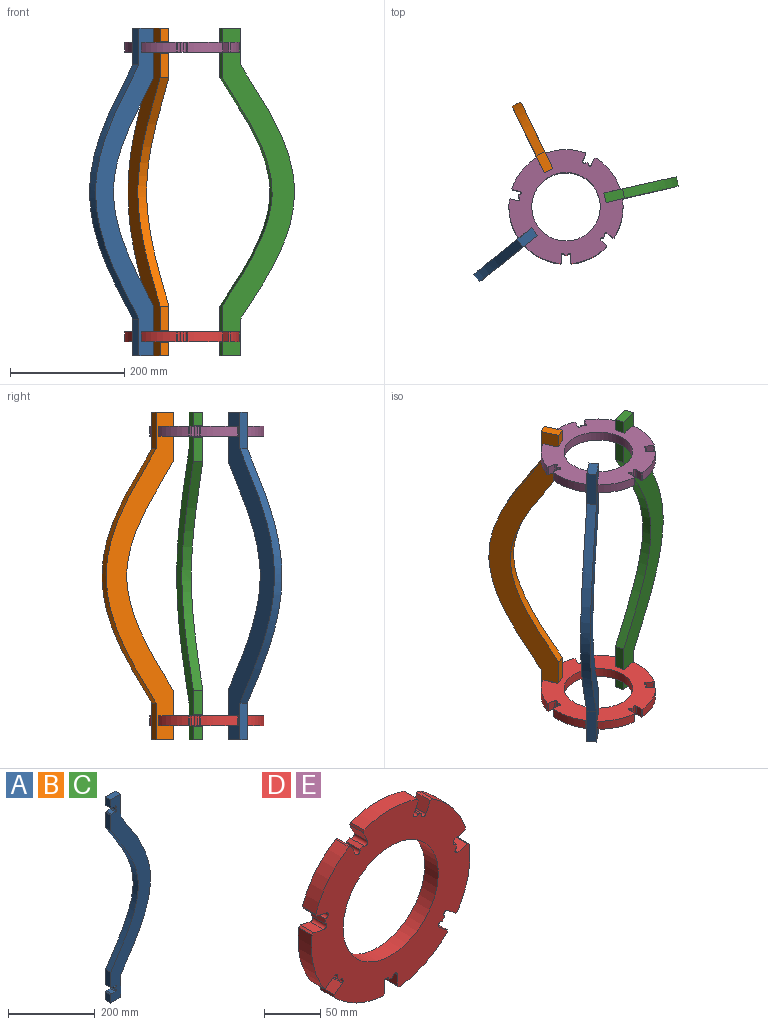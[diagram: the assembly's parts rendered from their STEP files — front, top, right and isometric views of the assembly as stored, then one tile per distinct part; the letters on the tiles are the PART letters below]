
ASSEMBLY  parts=5 mates=12
PART A: 26 faces, bbox 130x17x573.6 mm
  f0: plane 17x4.8mm, normal (-1,0,0), area 81.6mm2, adj f2,f3,f18,f19
  f1: plane 17x4.8mm, normal (-1,0,0), area 81.6mm2, adj f2,f3,f20,f21
  f2: plane 573.6x130.01mm, normal (0,-1,0), area 23198mm2, adj f0,f1,f4,f5,f6,f7,f8,f9
  f3: plane 573.6x130.01mm, normal (0,1,0), area 23198mm2, adj f0,f1,f4,f5,f6,f7,f8,f9
  f4: plane 33.15x17mm, normal (0,0,1), area 563.6mm2, adj f2,f3,f5,f17
  f5: plane 23x17mm, normal (-1,0,0), area 391mm2, adj f2,f3,f4,f25
  f6: plane 17x13mm, normal (0,0,-1), area 221mm2, adj f2,f3,f19,f25
  f7: plane 17x13mm, normal (0,0,1), area 221mm2, adj f2,f3,f18,f24
  f8: plane 43x17mm, normal (-1,0,0), area 731mm2, adj f2,f3,f9,f24
  f9: extruded ~400x90mm, area 7565.6mm2, adj f2,f3,f8,f10
  f10: plane 43x17mm, normal (-1,0,0), area 731mm2, adj f2,f3,f9,f23
  f11: plane 17x13mm, normal (0,0,-1), area 221mm2, adj f2,f3,f20,f23
  f12: plane 17x13mm, normal (0,0,1), area 221mm2, adj f2,f3,f21,f22
  f13: plane 23x17mm, normal (-1,0,0), area 391mm2, adj f2,f3,f14,f22
  f14: plane 33.15x17mm, normal (0,0,-1), area 563.6mm2, adj f2,f3,f13,f15
  f15: plane 64.42x17mm, normal (1,0,0), area 1095.2mm2, adj f2,f3,f14,f16
  f16: extruded ~444.76x96.85mm, area 8370.8mm2, adj f2,f3,f15,f17
  f17: plane 64.42x17mm, normal (1,0,0), area 1095.2mm2, adj f2,f3,f4,f16
  f18: cylinder r=3mm len=17mm, axis (0,-1,0), area 160.2mm2, adj f0,f2,f3,f7
  f19: cylinder r=3mm len=17mm, axis (0,-1,0), area 160.2mm2, adj f0,f2,f3,f6
  f20: cylinder r=3mm len=17mm, axis (0,-1,0), area 160.2mm2, adj f1,f2,f3,f11
  f21: cylinder r=3mm len=17mm, axis (0,-1,0), area 160.2mm2, adj f1,f2,f3,f12
  f22: plane 17x2mm, normal (-0.71,0,0.71), area 48.1mm2, adj f2,f3,f12,f13
  f23: plane 17x2mm, normal (-0.71,0,-0.71), area 48.1mm2, adj f2,f3,f10,f11
  f24: plane 17x2mm, normal (-0.71,0,0.71), area 48.1mm2, adj f2,f3,f7,f8
  f25: plane 17x2mm, normal (-0.71,0,-0.71), area 48.1mm2, adj f2,f3,f5,f6
PART B: same geometry as A
PART C: same geometry as A
PART D: 59 faces, bbox 200x17x199.5 mm
  f0: plane 17x3.75mm, normal (-0.78,0,-0.62), area 81.6mm2, adj f7,f8,f51,f58
  f1: plane 17x4.8mm, normal (0,0,-1), area 81.6mm2, adj f7,f8,f56,f57
  f2: plane 17x3.75mm, normal (0.78,0,-0.62), area 81.6mm2, adj f7,f8,f49,f55
  f3: plane 17x4.68mm, normal (0.97,0,0.22), area 81.6mm2, adj f7,f8,f47,f48
  f4: plane 17x4.32mm, normal (0.43,0,0.9), area 81.6mm2, adj f7,f8,f46,f50
  f5: plane 17x4.32mm, normal (-0.43,0,0.9), area 81.6mm2, adj f7,f8,f45,f54
  f6: plane 17x4.68mm, normal (-0.97,0,0.22), area 81.6mm2, adj f7,f8,f52,f53
  f7: plane 200x199.45mm, normal (0,-1,0), area 18129.3mm2, adj f0,f1,f2,f3,f4,f5,f6,f9
  f8: plane 200x199.45mm, normal (0,1,0), area 18129.3mm2, adj f0,f1,f2,f3,f4,f5,f6,f9
  f9: plane 17x12.31mm, normal (0.22,0,0.97), area 214.6mm2, adj f7,f8,f31,f53
  f10: cylinder r=100mm len=65.82mm, axis (0,1,0), area 1170.6mm2, adj f7,f8,f31,f33
  f11: plane 17x9.87mm, normal (0.62,0,-0.78), area 214.6mm2, adj f7,f8,f33,f58
  f12: plane 17x9.87mm, normal (-0.62,0,0.78), area 214.6mm2, adj f7,f8,f34,f51
  f13: cylinder r=100mm len=60.82mm, axis (0,1,0), area 1170.6mm2, adj f7,f8,f34,f35
  f14: plane 17x12.63mm, normal (1,0,0), area 214.6mm2, adj f7,f8,f35,f56
  f15: plane 17x12.63mm, normal (-1,0,0), area 214.6mm2, adj f7,f8,f36,f57
  f16: cylinder r=100mm len=60.82mm, axis (0,1,0), area 1170.6mm2, adj f7,f8,f36,f37
  f17: plane 17x9.87mm, normal (0.62,0,0.78), area 214.6mm2, adj f7,f8,f37,f49
  f18: plane 17x9.87mm, normal (-0.62,0,-0.78), area 214.6mm2, adj f7,f8,f38,f55
  f19: cylinder r=100mm len=65.82mm, axis (0,1,0), area 1170.6mm2, adj f7,f8,f38,f39
  f20: plane 17x12.31mm, normal (-0.22,0,0.97), area 214.6mm2, adj f7,f8,f39,f47
  f21: plane 17x12.31mm, normal (0.22,0,-0.97), area 214.6mm2, adj f7,f8,f40,f48
  f22: cylinder r=100mm len=52.78mm, axis (0,1,0), area 1170.6mm2, adj f7,f8,f40,f41
  f23: plane 17x11.38mm, normal (-0.9,0,0.43), area 214.6mm2, adj f7,f8,f41,f50
  f24: plane 17x11.38mm, normal (0.9,0,-0.43), area 214.6mm2, adj f7,f8,f42,f46
  f25: cylinder r=100mm len=67.51mm, axis (0,1,0), area 1170.6mm2, adj f7,f8,f42,f43
  f26: plane 17x11.38mm, normal (-0.9,0,-0.43), area 214.6mm2, adj f7,f8,f43,f54
  f27: plane 17x11.38mm, normal (0.9,0,0.43), area 214.6mm2, adj f7,f8,f44,f45
  f28: cylinder r=100mm len=52.78mm, axis (0,1,0), area 1170.6mm2, adj f7,f8,f32,f44
  f29: plane 17x12.31mm, normal (-0.22,0,-0.97), area 214.6mm2, adj f7,f8,f32,f52
  f30: cylinder r=60mm len=120mm, axis (0,1,0), area 6408.8mm2, adj f7,f8
  f31: plane 17x2.23mm, normal (-0.58,0,0.82), area 46.4mm2, adj f7,f8,f9,f10
  f32: plane 17x2.39mm, normal (-0.87,0,-0.49), area 46.4mm2, adj f7,f8,f28,f29
  f33: plane 17x2.7mm, normal (-0.16,0,-0.99), area 46.4mm2, adj f7,f8,f10,f11
  f34: plane 17x2.73mm, normal (-1,0,0.06), area 46.4mm2, adj f7,f8,f12,f13
  f35: plane 17x2.03mm, normal (0.67,0,-0.74), area 46.4mm2, adj f7,f8,f13,f14
  f36: plane 17x2.03mm, normal (-0.67,0,-0.74), area 46.4mm2, adj f7,f8,f15,f16
  f37: plane 17x2.73mm, normal (1,0,0.06), area 46.4mm2, adj f7,f8,f16,f17
  f38: plane 17x2.7mm, normal (0.16,0,-0.99), area 46.4mm2, adj f7,f8,f18,f19
  f39: plane 17x2.23mm, normal (0.58,0,0.82), area 46.4mm2, adj f7,f8,f19,f20
  f40: plane 17x2.39mm, normal (0.87,0,-0.49), area 46.4mm2, adj f7,f8,f21,f22
  f41: plane 17x2.62mm, normal (-0.28,0,0.96), area 46.4mm2, adj f7,f8,f22,f23
  f42: plane 17x2.53mm, normal (0.93,0,0.38), area 46.4mm2, adj f7,f8,f24,f25
  f43: plane 17x2.53mm, normal (-0.93,0,0.38), area 46.4mm2, adj f7,f8,f25,f26
  f44: plane 17x2.62mm, normal (0.28,0,0.96), area 46.4mm2, adj f7,f8,f27,f28
  f45: cylinder r=3mm len=17mm, axis (0,-1,0), area 160.2mm2, adj f5,f7,f8,f27
  f46: cylinder r=3mm len=17mm, axis (0,-1,0), area 160.2mm2, adj f4,f7,f8,f24
  f47: cylinder r=3mm len=17mm, axis (0,-1,0), area 160.2mm2, adj f3,f7,f8,f20
  f48: cylinder r=3mm len=17mm, axis (0,-1,0), area 160.2mm2, adj f3,f7,f8,f21
  f49: cylinder r=3mm len=17mm, axis (0,-1,0), area 160.2mm2, adj f2,f7,f8,f17
  f50: cylinder r=3mm len=17mm, axis (0,-1,0), area 160.2mm2, adj f4,f7,f8,f23
  f51: cylinder r=3mm len=17mm, axis (0,-1,0), area 160.2mm2, adj f0,f7,f8,f12
  f52: cylinder r=3mm len=17mm, axis (0,-1,0), area 160.2mm2, adj f6,f7,f8,f29
  f53: cylinder r=3mm len=17mm, axis (0,-1,0), area 160.2mm2, adj f6,f7,f8,f9
  f54: cylinder r=3mm len=17mm, axis (0,-1,0), area 160.2mm2, adj f5,f7,f8,f26
  f55: cylinder r=3mm len=17mm, axis (0,-1,0), area 160.2mm2, adj f2,f7,f8,f18
  f56: cylinder r=3mm len=17mm, axis (0,-1,0), area 160.2mm2, adj f1,f7,f8,f14
  f57: cylinder r=3mm len=17mm, axis (0,-1,0), area 160.2mm2, adj f1,f7,f8,f15
  f58: cylinder r=3mm len=17mm, axis (0,-1,0), area 160.2mm2, adj f0,f7,f8,f11
PART E: same geometry as D
PLACE A rot(axis=(0,0,-1),141.4deg) t=(-365.21,-119.31,119.36)mm
PLACE B rot(axis=(0,0,1),115.7deg) t=(-353.84,-9.76,119.36)mm
PLACE C rot(axis=(0,0,1),12.9deg) t=(-249.39,-45.14,119.36)mm
PLACE D rot(axis=(-0.83,-0.4,0.4),100.9deg) t=(-315.72,-69.1,-142.44)mm
PLACE E rot(axis=(-1,0,0),90deg) t=(-315.72,-69.1,364.16)mm
MATE planar B.f2 <-> E.f26  axis (0.9,0.43,0) through (-352.91,27.49,341.74)mm
MATE planar C.f2 <-> E.f20  axis (0.22,-0.97,0) through (-213.28,-54.33,341.74)mm
MATE planar C.f6 <-> E.f7  axis (0,0,-1) through (-239.21,-51.53,381.16)mm
MATE planar A.f3 <-> E.f12  axis (0.62,-0.78,0) through (-376.94,-128.66,364.36)mm
MATE planar B.f6 <-> E.f7  axis (0,0,-1) through (-357.53,-2.1,381.16)mm
MATE planar C.f0 <-> E.f3  axis (-0.97,-0.22,0) through (-232.87,-50.09,372.76)mm
MATE planar D.f9 <-> A.f3  axis (-0.62,0.78,0) through (-381.87,-132.6,-133.94)mm
MATE planar D.f8 <-> A.f12  axis (0,0,-1) through (-376.94,-128.66,-142.44)mm
MATE cylindrical D.f10 <-> E.f10  axis (0,0,-1) through (-315.72,-69.1,-133.94)mm
MATE planar B.f0 <-> E.f5  axis (0.43,-0.9,0) through (-352.69,7.44,372.76)mm
MATE planar A.f6 <-> E.f7  axis (0,0,-1) through (-377.15,-117.96,381.16)mm
MATE planar A.f0 <-> E.f0  axis (0.78,0.62,0) through (-382.24,-122.02,372.76)mm
